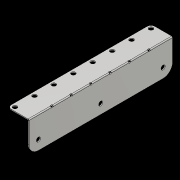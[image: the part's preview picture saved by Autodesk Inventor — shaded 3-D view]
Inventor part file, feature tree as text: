
AUTODESK INVENTOR PART (.ipt)
format: ipt  version: 2018.2 (Build 222227000, 227)  size: 380,928 bytes
history: native  units: mm
features: other x8, sketch x4, extrude x2, fillet x1, projected_geometry x1
ambient origin geometry x8: Origin, YZ Plane, XZ Plane, XY Plane, X Axis, Y Axis, Z Axis, Center Point
bodies: Body1 (feature_tree)
feature tree (16):
  other  "ソリッド1"
  other  "フランジ1"
  extrude  "押し出し1"  Depth=151.5mm
  fillet  "フィレット1"  Radius=21.777mm
  other  "展開1"
  extrude  "押し出し2"  Depth=4.5mm
  other  "再折り曲げ1"
  sketch  "スケッチ1"
  other  "プレート1"
  sketch  "スケッチ2"
  other  "プレート2"
  other  "曲げ1"
  other  "コーナー1"
  sketch  "スケッチ3"
  sketch  "スケッチ4"
  projected_geometry  "投影ループ1"
